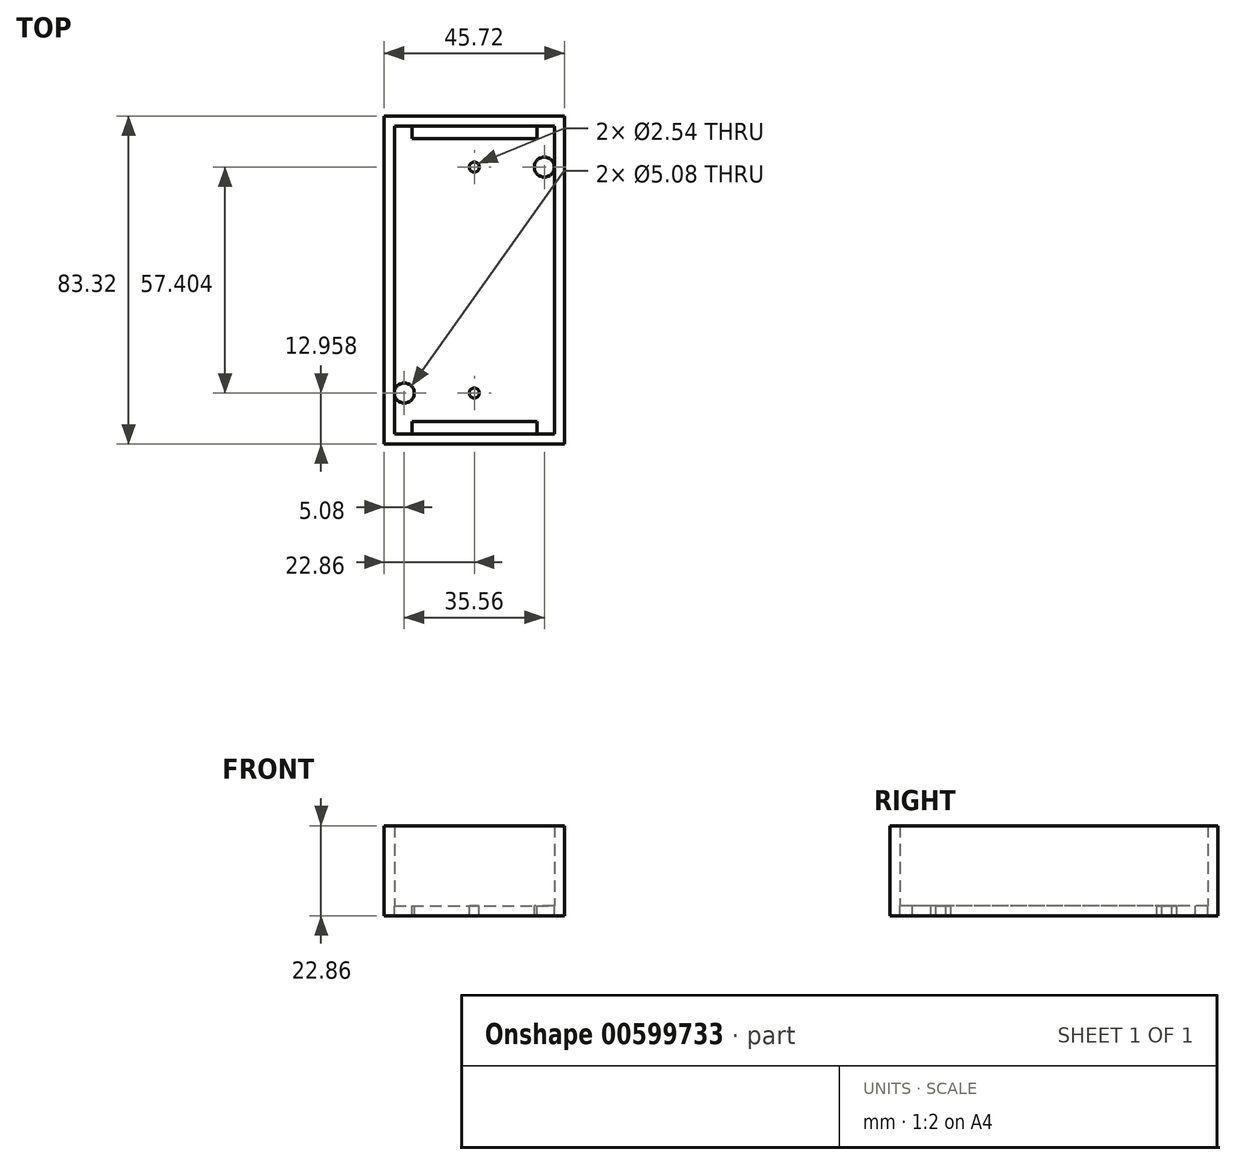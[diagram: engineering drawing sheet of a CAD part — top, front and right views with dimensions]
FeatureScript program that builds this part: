
annotation { "Feature Type Name" : "Feature", "Feature Type Description" : "" }
export const myFeature = defineFeature(function(context is Context, id is Id, definition is map)
    precondition{}
    {
        {
            var Q0;
            Q0=qCreatedBy(makeId("Top.planeOp"),FACE);
            var sketch = newSketch(context, id + "F0", { "sketchPlane" : qUnion([Q0])});
            skLineSegment(sketch, "E0.bottom", {"start": v(-22.86, 41.66) * mm, "end": v(22.86, 41.66) * mm});
            skLineSegment(sketch, "E0.top", {"start": v(-22.86, -41.66) * mm, "end": v(22.86, -41.66) * mm});
            skLineSegment(sketch, "E0.left", {"start": v(-22.86, 41.66) * mm, "end": v(-22.86, -41.66) * mm});
            skLineSegment(sketch, "E0.right", {"start": v(22.86, 41.66) * mm, "end": v(22.86, -41.66) * mm});
            skPoint(sketch, "E0.middle", {"position": v(0, 0) * mm});
            skSolve(sketch);
        }
        {
            var Q0;
            Q0 = qSketchRegion(id + "F0", true);
            extrude(context, id + "F1", {"entities" : qUnion([Q0]), "depth" : 2.54 * mm, "offsetDistance" : 25.4 * mm});
        }
        {
            var Q0;
            Q0=makeQuery(id+"F1.opExtrude","CAP_FACE",FACE,{"disambiguationData":[OSD([sQuery(id+"F0.wireOp",EDGE,"E0.bottom"),sQuery(id+"F0.wireOp",EDGE,"E0.top"),sQuery(id+"F0.wireOp",EDGE,"E0.left"),sQuery(id+"F0.wireOp",EDGE,"E0.right")])],"isStart":false});
            var sketch = newSketch(context, id + "F2", { "sketchPlane" : qUnion([Q0])});
            skLineSegment(sketch, "E1.bottom", {"start": v(-22.86, 41.66) * mm, "end": v(22.86, 41.66) * mm});
            skLineSegment(sketch, "E1.top", {"start": v(-22.86, -41.66) * mm, "end": v(22.86, -41.66) * mm});
            skLineSegment(sketch, "E1.left", {"start": v(-22.86, 41.66) * mm, "end": v(-22.86, -41.66) * mm});
            skLineSegment(sketch, "E1.right", {"start": v(22.86, 41.66) * mm, "end": v(22.86, -41.66) * mm});
            skPoint(sketch, "E1.middle", {"position": v(0, 0) * mm});
            skLineSegment(sketch, "E2.bottom", {"start": v(-20.32, 39.12) * mm, "end": v(20.32, 39.12) * mm});
            skLineSegment(sketch, "E2.top", {"start": v(-20.32, -39.12) * mm, "end": v(20.32, -39.12) * mm});
            skLineSegment(sketch, "E2.left", {"start": v(-20.32, 39.12) * mm, "end": v(-20.32, -39.12) * mm});
            skLineSegment(sketch, "E2.right", {"start": v(20.32, 39.12) * mm, "end": v(20.32, -39.12) * mm});
            skSolve(sketch);
        }
        {
            var Q0;
            Q0 = qSketchRegion(id + "F2", true);
            extrude(context, id + "F3", {"entities" : qUnion([Q0]), "operationType" : NewBodyOperationType.ADD, "depth" : 20.32 * mm, "offsetDistance" : 25.4 * mm});
        }
        {
            var Q0;
            Q0=makeQuery(id+"F1.opExtrude","CAP_FACE",FACE,{"disambiguationData":[OSD([sQuery(id+"F0.wireOp",EDGE,"E0.bottom"),sQuery(id+"F0.wireOp",EDGE,"E0.top"),sQuery(id+"F0.wireOp",EDGE,"E0.left"),sQuery(id+"F0.wireOp",EDGE,"E0.right")])],"isStart":false});
            var sketch = newSketch(context, id + "F4", { "sketchPlane" : qUnion([Q0])});
            skCircle(sketch, "E3", {"center": v(0, 28.7) * mm, "radius": 1.27 * mm});
            skCircle(sketch, "E4", {"center": v(0, -28.7) * mm, "radius": 1.27 * mm});
            skCircle(sketch, "E5", {"center": v(17.78, 28.7) * mm, "radius": 2.54 * mm});
            skCircle(sketch, "E6", {"center": v(-17.78, -28.7) * mm, "radius": 2.54 * mm});
            skLineSegment(sketch, "E7", {"start": v(-17.78, -28.7) * mm, "end": v(0, -28.7) * mm, "construction": true});
            skLineSegment(sketch, "E8", {"start": v(0, 28.7) * mm, "end": v(17.78, 28.7) * mm, "construction": true});
            skLineSegment(sketch, "E9.bottom", {"start": v(-15.87, 39.12) * mm, "end": v(15.88, 39.12) * mm});
            skLineSegment(sketch, "E9.top", {"start": v(-15.87, 35.94) * mm, "end": v(15.88, 35.94) * mm});
            skLineSegment(sketch, "E9.left", {"start": v(-15.87, 39.12) * mm, "end": v(-15.87, 35.94) * mm});
            skLineSegment(sketch, "E9.right", {"start": v(15.88, 39.12) * mm, "end": v(15.88, 35.94) * mm});
            skPoint(sketch, "E9.middle", {"position": v(0, 37.53) * mm});
            skLineSegment(sketch, "E10.bottom", {"start": v(-15.88, -35.94) * mm, "end": v(15.88, -35.94) * mm});
            skLineSegment(sketch, "E10.top", {"start": v(-15.88, -39.12) * mm, "end": v(15.88, -39.12) * mm});
            skLineSegment(sketch, "E10.left", {"start": v(-15.88, -35.94) * mm, "end": v(-15.88, -39.12) * mm});
            skLineSegment(sketch, "E10.right", {"start": v(15.88, -35.94) * mm, "end": v(15.88, -39.12) * mm});
            skPoint(sketch, "E10.middle", {"position": v(0, -37.53) * mm});
            skLineSegment(sketch, "E11", {"start": v(0, 37.53) * mm, "end": v(0, 39.12) * mm, "construction": true});
            skLineSegment(sketch, "E12", {"start": v(0, -39.12) * mm, "end": v(0, -37.53) * mm, "construction": true});
            skSolve(sketch);
        }
        {
            var Q0;
            Q0 = qSketchRegion(id + "F4", true);
            extrude(context, id + "F5", {"entities" : qUnion([Q0]), "operationType" : NewBodyOperationType.REMOVE, "oppositeDirection" : true, "depth" : 25.4 * mm, "offsetDistance" : 25.4 * mm});
        }
    });
